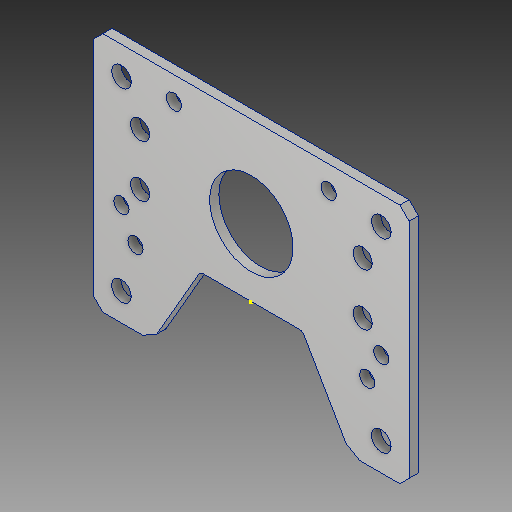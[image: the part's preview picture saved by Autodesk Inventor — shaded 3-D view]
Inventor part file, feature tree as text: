
AUTODESK INVENTOR PART (.ipt)
format: ipt  version: 2017 (Build 210142000, 142)  size: 177,152 bytes
history: native  units: in
note: dims shown in document units (in); Inventor stores cm internally (conversion verified against a paired STEP export)
features: sketch x3, extrude x1, fillet x1
ambient origin geometry x8: Origin, YZ Plane, XZ Plane, XY Plane, X Axis, Y Axis, Z Axis, Center Point
bodies: Solid1 (feature_tree)
feature tree (5):
  sketch  "Sketch1"  dims[d8=1.5in d9=0.35in d10=0.35in]
  sketch  "Sketch2"  dims[d11=1.5in]
  sketch  "Sketch3"  dims[d12=0.35in d13=0.35in d14=0.257in d15=0.257in d16=0.257in d17=0.257in d18=1.0in d19=0.0in]
  extrude  "Extrusion2"  Depth=0.35in
  fillet  "Fillet1"  Radius=0.35in
